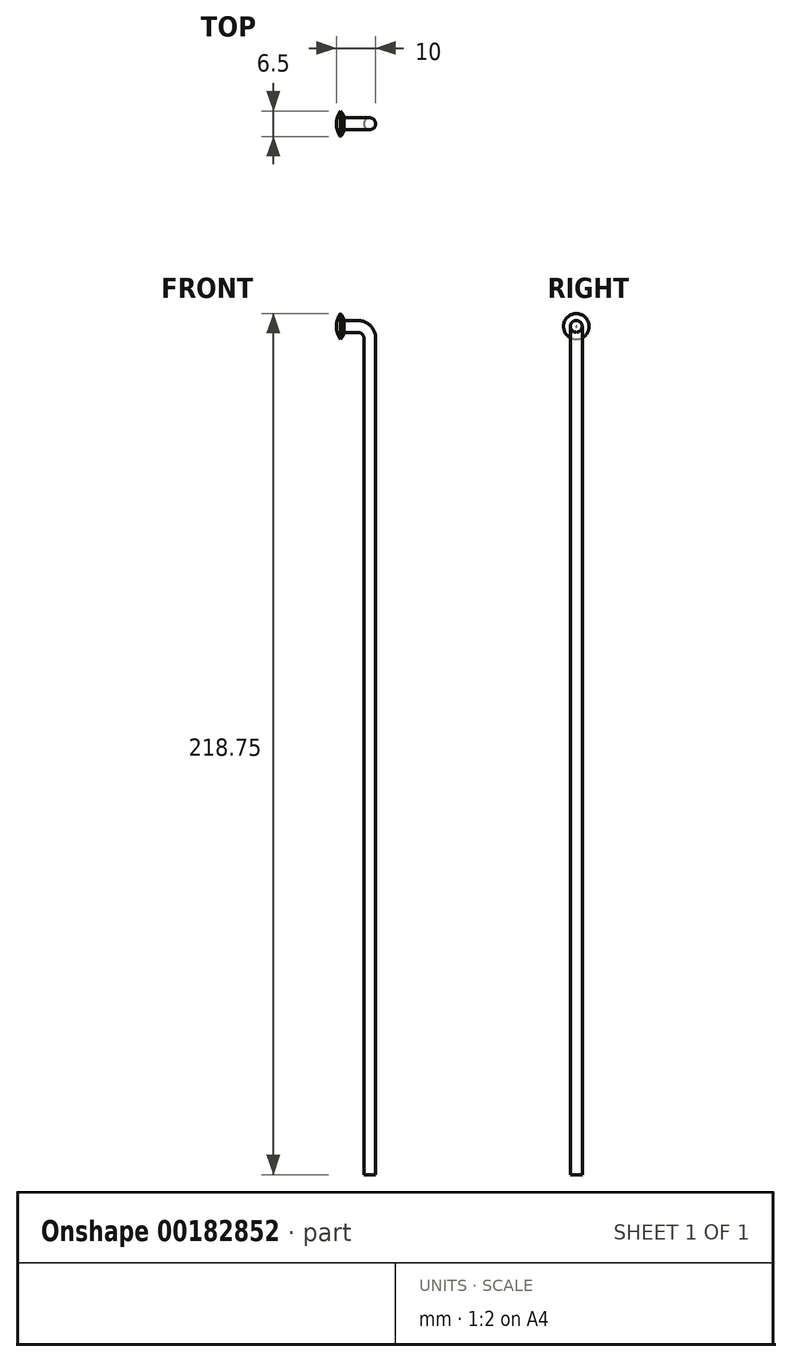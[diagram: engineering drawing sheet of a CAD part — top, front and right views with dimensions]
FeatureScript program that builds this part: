
annotation { "Feature Type Name" : "Feature", "Feature Type Description" : "" }
export const myFeature = defineFeature(function(context is Context, id is Id, definition is map)
    precondition{}
    {
        {
            var Q0;
            Q0=qCreatedBy(makeId("Right.planeOp"),FACE);
            var sketch = newSketch(context, id + "F0", { "sketchPlane" : qUnion([Q0])});
            skCircle(sketch, "E0", {"center": v(0, 0) * mm, "radius": 1.5 * mm});
            skSolve(sketch);
        }
        {
            var Q0;
            Q0=qCreatedBy(makeId("Front.planeOp"),FACE);
            var sketch = newSketch(context, id + "F1", { "sketchPlane" : qUnion([Q0])});
            skLineSegment(sketch, "E1", {"start": v(0, 0) * mm, "end": v(3.5, 0) * mm});
            skLineSegment(sketch, "E2", {"start": v(6.5, -3) * mm, "end": v(6.5, -215.5) * mm});
            skPoint(sketch, "E3.visualSharp", {"position": v(6.5, 0) * mm});
            skArc(sketch, "E3.filletArc", {"start": v(6.5, -3) * mm, "mid": v(5.62, -0.88) * mm, "end": v(3.5, 0) * mm});
            skSolve(sketch);
        }
        {
            var Q0;
            Q0=makeQuery(id+"F0.imprint","IMPRINT",FACE,{"disambiguationData":[TD([[makeQuery(id+"F0.imprint","IMPRINT",EDGE,{"derivedFrom":sQuery(id+"F0.wireOp",EDGE,"E0")}),1.0]])]});
            var Q1;
            Q1=sQuery(id+"F1.wireOp",EDGE,"E1");
            var Q2;
            Q2=sQuery(id+"F1.wireOp",EDGE,"E3.filletArc");
            var Q3;
            Q3=sQuery(id+"F1.wireOp",EDGE,"E2");
            sweep(context, id + "F2", {"profiles" : qUnion([Q0]), "path" : qUnion([Q1, Q2, Q3])});
        }
        {
            var Q0;
            Q0=qCreatedBy(makeId("Front.planeOp"),FACE);
            var sketch = newSketch(context, id + "F3", { "sketchPlane" : qUnion([Q0])});
            skLineSegment(sketch, "E4", {"start": v(0, 0) * mm, "end": v(-2, 0) * mm});
            skLineSegment(sketch, "E5", {"start": v(-1, 0) * mm, "end": v(-1, 3.25) * mm});
            skArc(sketch, "E6", {"start": v(0, 1.5) * mm, "mid": v(-0.35, 2.46) * mm, "end": v(-1, 3.25) * mm});
            skArc(sketch, "E7", {"start": v(-1, 3.25) * mm, "mid": v(-1.74, 1.7) * mm, "end": v(-2, 0) * mm});
            skLineSegment(sketch, "E8", {"start": v(0, 1.5) * mm, "end": v(0, 0) * mm});
            skSolve(sketch);
        }
        {
            var Q0;
            Q0 = qSketchRegion(id + "F3", true);
            var Q1;
            Q1=sQuery(id+"F3.wireOp",EDGE,"E4");
            revolve(context, id + "F4", {"operationType" : NewBodyOperationType.ADD, "entities" : qUnion([Q0]), "axis" : qUnion([Q1]), "revolveType" : RevolveType.FULL});
        }
    });
